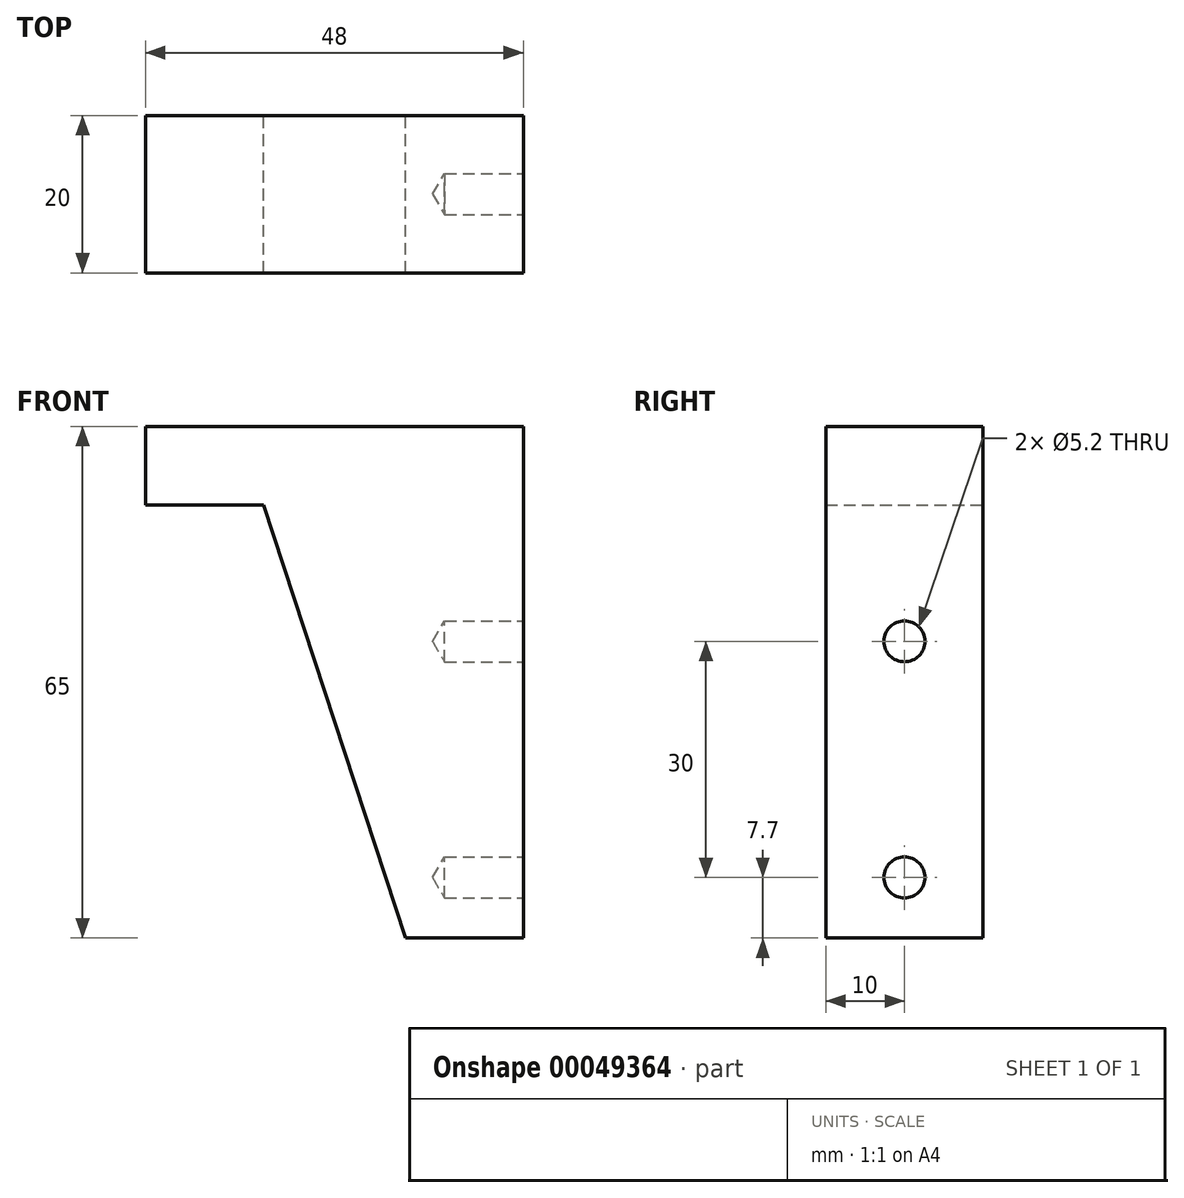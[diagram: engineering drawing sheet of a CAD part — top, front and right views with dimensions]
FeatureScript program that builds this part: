
annotation { "Feature Type Name" : "Feature", "Feature Type Description" : "" }
export const myFeature = defineFeature(function(context is Context, id is Id, definition is map)
    precondition{}
    {
        {
            var Q0;
            Q0=qCreatedBy(makeId("Front.planeOp"),FACE);
            var sketch = newSketch(context, id + "F0", { "sketchPlane" : qUnion([Q0])});
            skLineSegment(sketch, "E0", {"start": v(0, 0) * mm, "end": v(0, -65) * mm});
            skLineSegment(sketch, "E1", {"start": v(0, -65) * mm, "end": v(-15, -65) * mm});
            skLineSegment(sketch, "E2", {"start": v(-15, -65) * mm, "end": v(-33, -10) * mm});
            skLineSegment(sketch, "E3", {"start": v(-33, -10) * mm, "end": v(-48, -10) * mm});
            skLineSegment(sketch, "E4", {"start": v(-48, -10) * mm, "end": v(-48, 0) * mm});
            skLineSegment(sketch, "E5", {"start": v(-48, 0) * mm, "end": v(0, 0) * mm});
            skSolve(sketch);
        }
        {
            var Q0;
            Q0=makeQuery(id+"F0.imprint","IMPRINT",FACE,{"disambiguationData":[TD([[makeQuery(id+"F0.imprint","IMPRINT",EDGE,{"derivedFrom":sQuery(id+"F0.wireOp",EDGE,"E0")}),-1.0]])]});
            extrude(context, id + "F1", {"entities" : qUnion([Q0]), "depth" : 20 * mm});
        }
        {
            var Q0;
            Q0=makeQuery(id+"F1.opExtrude","SWEPT_FACE",FACE,{"disambiguationData":[OSD([sQuery(id+"F0.wireOp",EDGE,"E0")])]});
            var sketch = newSketch(context, id + "F2", { "sketchPlane" : qUnion([Q0])});
            skCircle(sketch, "E6", {"center": v(-10, -27.3) * mm, "radius": 2.7 * mm, "construction": true});
            skCircle(sketch, "E7", {"center": v(-10, -57.3) * mm, "radius": 2.7 * mm, "construction": true});
            skLineSegment(sketch, "E8", {"start": v(-10, -27.3) * mm, "end": v(-10, -57.3) * mm, "construction": true});
            skLineSegment(sketch, "E9", {"start": v(-10, -57.3) * mm, "end": v(-10, -65) * mm, "construction": true});
            skSolve(sketch);
        }
        {
            var Q0;
            Q0=sQuery(id+"F2.wireOp",VERTEX,"E6.center");
            var Q1;
            Q1=sQuery(id+"F2.wireOp",VERTEX,"E7.center");
            var Q2;
            Q2=makeQuery(id+"F1.opExtrude","SWEPT_BODY",BODY,{"disambiguationData":[OSD([sQuery(id+"F0.wireOp",EDGE,"E0"),sQuery(id+"F0.wireOp",EDGE,"E1"),sQuery(id+"F0.wireOp",EDGE,"E2"),sQuery(id+"F0.wireOp",EDGE,"E3"),sQuery(id+"F0.wireOp",EDGE,"E4"),sQuery(id+"F0.wireOp",EDGE,"E5")])]});
            hole(context, id + "F3", {"style" : HoleStyle.SIMPLE, "holeDiameter" : 5.2 * mm, "endStyle" : HoleEndStyle.BLIND, "holeDepth" : 10 * mm, "locations" : qUnion([Q0, Q1]), "scope" : qUnion([Q2])});
        }
    });
